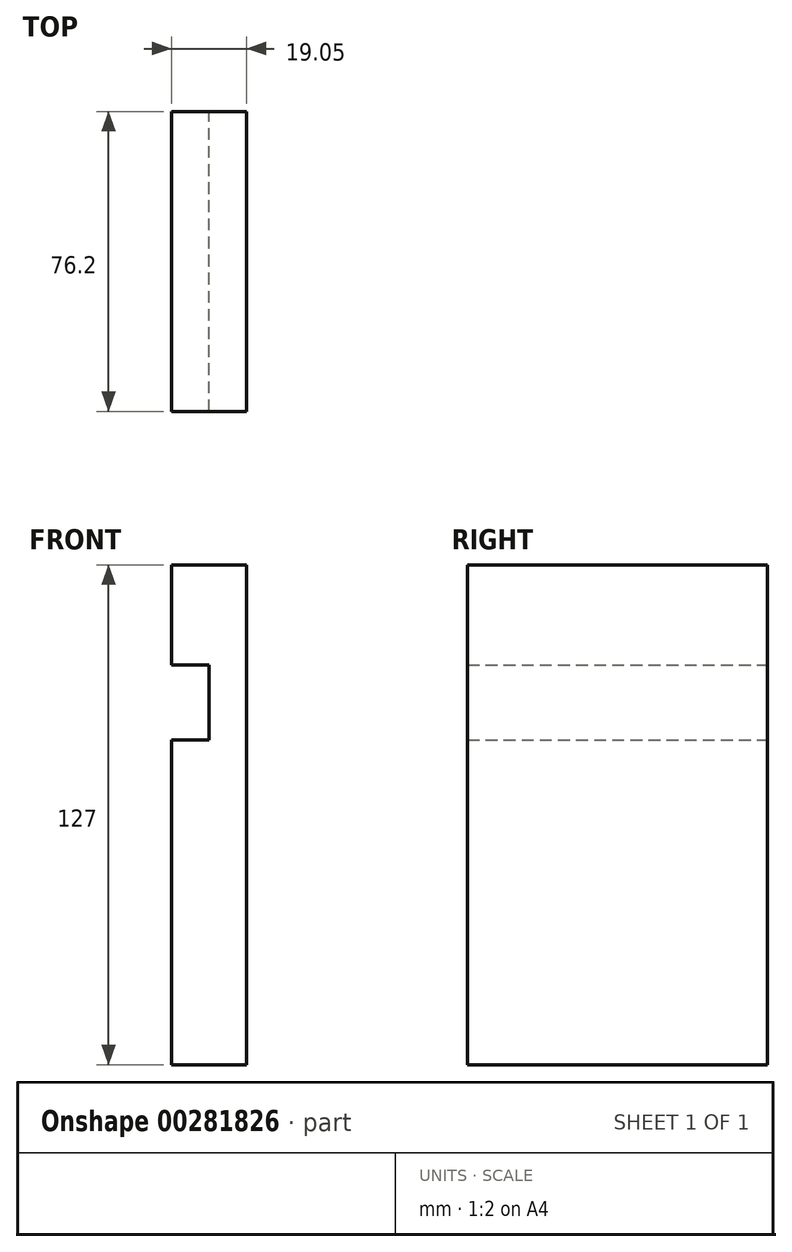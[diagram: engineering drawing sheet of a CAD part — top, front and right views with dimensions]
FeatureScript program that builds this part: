
annotation { "Feature Type Name" : "Feature", "Feature Type Description" : "" }
export const myFeature = defineFeature(function(context is Context, id is Id, definition is map)
    precondition{}
    {
        {
            var Q0;
            Q0=qCreatedBy(makeId("Front.planeOp"),FACE);
            var sketch = newSketch(context, id + "F0", { "sketchPlane" : qUnion([Q0])});
            skLineSegment(sketch, "E0", {"start": v(0, 0) * mm, "end": v(19.05, 0) * mm});
            skLineSegment(sketch, "E1", {"start": v(19.05, 0) * mm, "end": v(19.05, 127) * mm});
            skLineSegment(sketch, "E2", {"start": v(19.05, 127) * mm, "end": v(0, 127) * mm});
            skLineSegment(sketch, "E3", {"start": v(0, 127) * mm, "end": v(0, 101.6) * mm});
            skLineSegment(sketch, "E4", {"start": v(0, 101.6) * mm, "end": v(9.53, 101.6) * mm});
            skLineSegment(sketch, "E5", {"start": v(9.53, 101.6) * mm, "end": v(9.53, 82.55) * mm});
            skLineSegment(sketch, "E6", {"start": v(9.53, 82.55) * mm, "end": v(0, 82.55) * mm});
            skLineSegment(sketch, "E7", {"start": v(0, 82.55) * mm, "end": v(0, 0) * mm});
            skSolve(sketch);
        }
        {
            var Q0;
            Q0=makeQuery(id+"F0.imprint","IMPRINT",FACE,{"disambiguationData":[TD([[makeQuery(id+"F0.imprint","IMPRINT",EDGE,{"derivedFrom":sQuery(id+"F0.wireOp",EDGE,"E0")}),1.0]])]});
            extrude(context, id + "F1", {"entities" : qUnion([Q0]), "depth" : 76.2 * mm});
        }
    });
